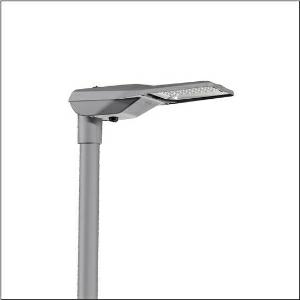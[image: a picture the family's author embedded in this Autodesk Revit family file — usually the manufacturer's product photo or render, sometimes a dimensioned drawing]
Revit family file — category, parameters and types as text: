
# Revit family: streetlight_sl_21_mini___st0_5a_5xe2b33t08hb_07ec
name_source: partatom
category: Lighting Fixtures
units: mm (PartAtom-declared; Revit-internal decimal feet)

## family parameters
Cut with Voids When Loaded = No
Host = Face
Light Source = No
Part Type = Normal
Room Calculation Point = No
Round Connector Dimension = Use Diameter
Shared = No

## types (1)
- --- (1 x LED, 9040 lm, 66 W, 3000K)
    Apparent Load = 66 VA
    CIE Flux Codes = 41 75 97 100 100
    Color Rendering = 70
    Color Temperature = 3000K
    Default Elevation = 1800 mm
    Description = Streetlight SL 21 mini, mast luminaire, primary light control with lens, of PMMA, primary optical cover: cover, of toughened safety glass, transparent, light distribution: ST0.5a, light emission: direct distribution, primary light characteristic: asymmetric, installation type: side-entry, post-top, LED, High Power LED, rated luminous flux: 9.040lm, luminous efficacy: 137lm/W, light colour: 730, colour temperature: 3000K, control gear: D4i, control: overheat protection, constant luminous flux control, time-dependent luminous flux control, flexible luminous flux parameterisation, pre-setting: logarithmic dimming characteristic, mains connection: 220..240V, AC, 50/60Hz, start of lifetime: 66W, end of service life: 69W, reduction: 30W, luminaire housing, of diecast aluminium, powder-coated, SITECO metallic grey (DB 702S), corrosivity category C5 high according to DIN EN ISO 12944, please order mast flange separately, inclination adjustable: 0°, 5°, 10°, 15°, sealing non-destructively replaceable, multi-level sealing system, length: 628mm, width: 235mm, height: 110mm, mast flange for spigot size: 42mm (side-entry): 5XC10008XM4, 60/48mm (side-entry/post-top): 5XC10108XM2, 76/60mm (side-entry/post-top): 5XC10108XM1, mounting height: 4..8m, Smart Interface below and above, protection rating (complete): IP66, insulation class (complete): insulation class II (safety insulation), certification: CE, ENEC, ENEC+, VDE, impact resistance: IK10, permissible operating ambient temperature for outdoor applications: -40..+50°C, standard-compliant lighting for roads and squares, packaging unit: 1 piece

Light Distribution: ST0.5a
    Height = 110 mm
    Lamp = 1 x LED
    Lamp Light Flux = 9040 lm
    Lamp Power = 66 W
    Lamp count = 1
    Length = 625 mm
    Luminous efficacy = 137 lm/W
    Manufacturer = Siteco
    ModVariant = No
    Model = 5XE2B33T08HB
    Number of Poles = 1
    OnlyDefault = Yes
    Power Factor = 1
    Product Name = Streetlight SL 21 mini | ST0.5a
    Product group = mast luminaire | pylon top
    ProductGroupID = 6100
    Protection Class = Protection class II
    Protection Degree = IP 66
    RLX_Detail_Level = 1
    RLX_Emergency_Light_Flux = 0 lm
    RLX_Emergency_Type = 0
    RLX_Emergency_Type_DB = No
    RlxData = <blob elided: 37369 chars, md5=3c0b29c5>
    Socket = socket
    Standby Power = 0 W
    System Light Flux = 9040 lm
    System Power = 66 W
    Type Comments = factory setting: luminous flux: 100 % | dim-lin: 254 | 670 mA
    Type Image = l_1003514.jpg
    URL = http://relux.com
    VarID = @adj_188503
    Voltage = 0 V
    Weight = 0.00 kg
    Width = 234 mm

## geometry (parser evidence)
native form markers: Blend x4, Sweep x11
no freeform markers — native parametric forms only
